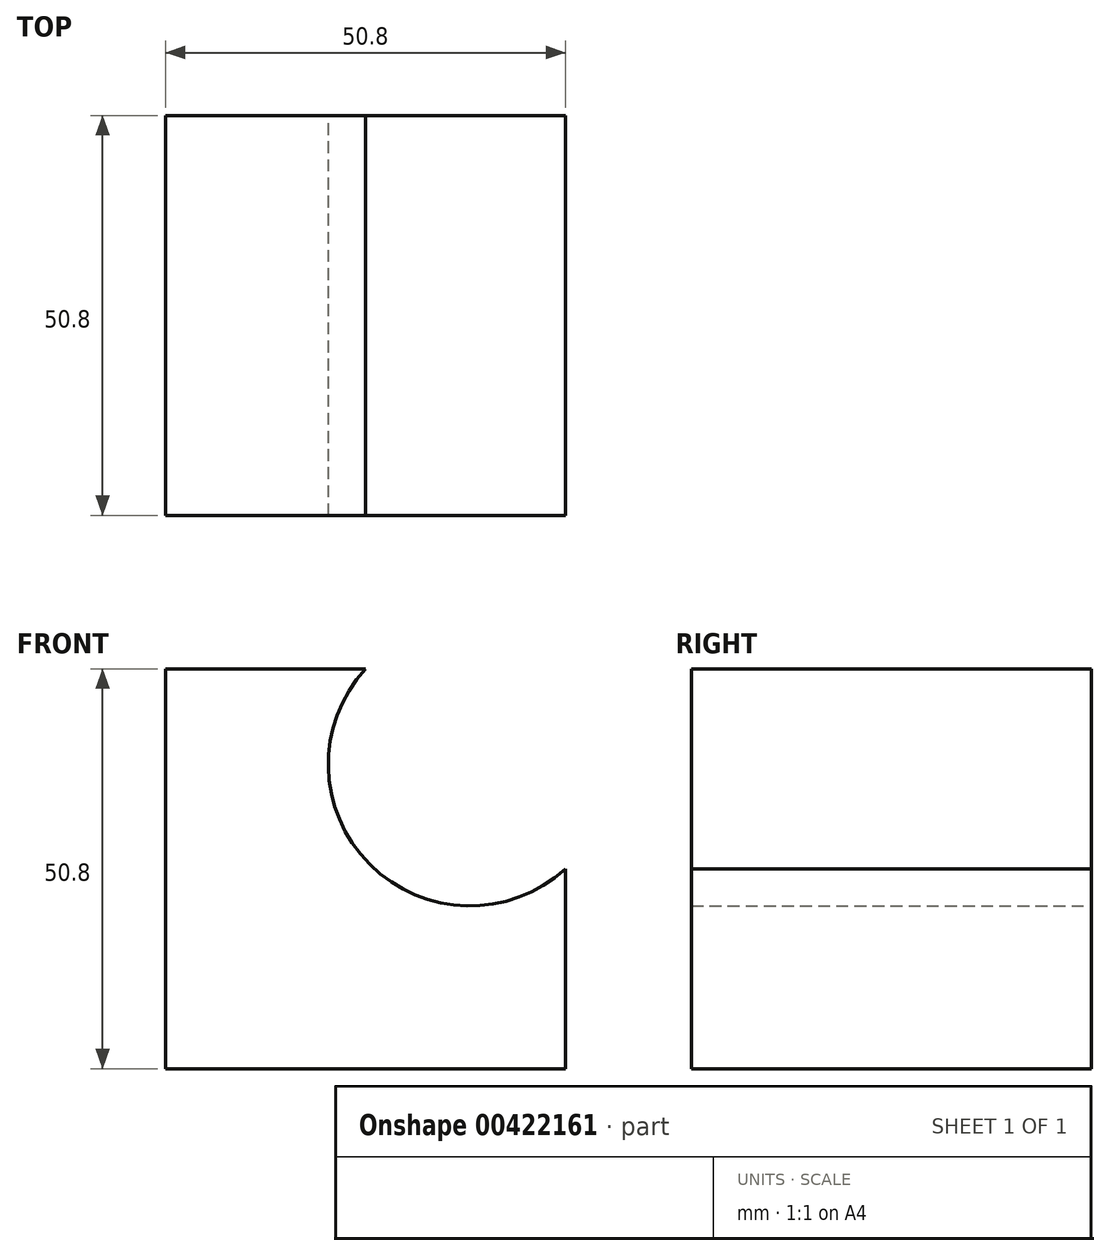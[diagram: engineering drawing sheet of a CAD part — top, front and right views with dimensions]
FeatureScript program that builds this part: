
annotation { "Feature Type Name" : "Feature", "Feature Type Description" : "" }
export const myFeature = defineFeature(function(context is Context, id is Id, definition is map)
    precondition{}
    {
        {
            var Q0;
            Q0=qCreatedBy(makeId("Front.planeOp"),FACE);
            var sketch = newSketch(context, id + "F0", { "sketchPlane" : qUnion([Q0])});
            skLineSegment(sketch, "E0", {"start": v(-7.35, 47.74) * mm, "end": v(-32.75, 47.74) * mm});
            skLineSegment(sketch, "E1", {"start": v(-32.75, 47.74) * mm, "end": v(-32.75, -3.06) * mm});
            skLineSegment(sketch, "E2", {"start": v(-32.75, -3.06) * mm, "end": v(18.05, -3.06) * mm});
            skLineSegment(sketch, "E3", {"start": v(18.05, -3.06) * mm, "end": v(18.05, 22.34) * mm});
            skArc(sketch, "E4", {"start": v(-7.35, 47.74) * mm, "mid": v(-6.81, 22.88) * mm, "end": v(18.05, 22.34) * mm});
            skSolve(sketch);
        }
        {
            var Q0;
            Q0 = qSketchRegion(id + "F0", true);
            extrude(context, id + "F1", {"entities" : qUnion([Q0]), "depth" : 50.8 * mm});
        }
    });
